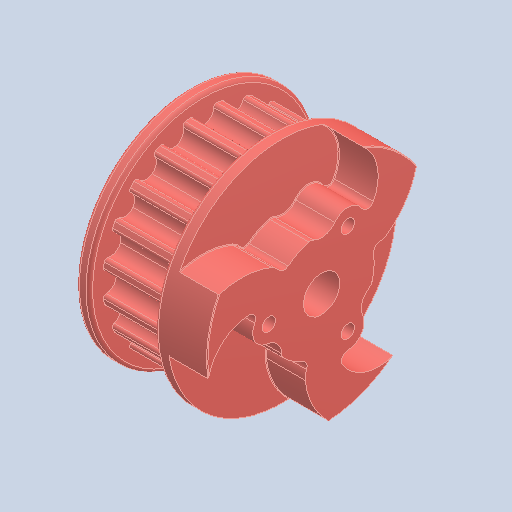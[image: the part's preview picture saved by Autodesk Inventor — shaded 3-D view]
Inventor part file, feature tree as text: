
AUTODESK INVENTOR PART (.ipt)
format: ipt  version: 2023.2 (Build 272271000, 271)  size: 845,312 bytes
history: native  units: in
note: dims shown in document units (in); Inventor stores cm internally (conversion verified against a paired STEP export)
features: extrude x4, sketch x4, other x4, thicken_offset x3, plane x2, fillet x2, chamfer x1, surface_op x1
ambient origin geometry x8: Origin, YZ Plane, XZ Plane, XY Plane, X Axis, Y Axis, Z Axis, Center Point
bodies: Solid1 (feature_tree), Body1 (feature_tree)
feature tree (21):
  extrude  "Extrusion1"  Depth=0.2165in
  plane  "Work Plane1"
  extrude  "Extrusion2"  [1 undecoded]
  chamfer  "Chamfer1"  Distance=0.3937in
  surface_op  "Sculpt1"
  extrude  "Extrusion3"  Depth=0.0039in
  sketch  "Sketch4"  dims[d8=0.0039in d9=0.0787in d10=45.0deg d11=0.2165in d12=1.1811in d14=360.0deg d16=0.0793in d17=0.0in d18=0.0in d19=1.378in d20=2.3622in d22=360.0deg d24=1.1811in d26=360.0deg d28=0.2362in d29=0.0in d32=0.0039in d33=0.0039in d34=0.0039in d35=0.0039in d36=0.0039in d37=0.0039in d38=0.0394in d39=0.0039in]
  plane  "Work Plane2"
  extrude  "Extrusion4"  Depth=0.0039in TaperAngle=360.0deg
  thicken_offset  "Thicken1"
  thicken_offset  "Thicken2"
  thicken_offset  "Thicken3"
  fillet  "Fillet3"  Radius=0.0793in
  fillet  "Fillet4"  [1 undecoded]
  sketch  "Sketch1"  dims[d0=0.4331in d1=0.2165in]
  sketch  "Sketch2"  dims[d2=0.3937in d3=0.0in d4=-0.0394in]
  sketch  "Sketch3"  dims[d5=1.3681in d6=0.3937in d7=0.0in]
  other  "Composite1"
  other  "Srf1"
  other  "Flash Hobby D3530 1100KV.iam"
  other  "Body - Basic:1"
note: 2 required parameter values undecoded (feature->parameter linkage not recoverable at this tier; creation-order binding heuristic only, values carry confidence <= 0.55)
